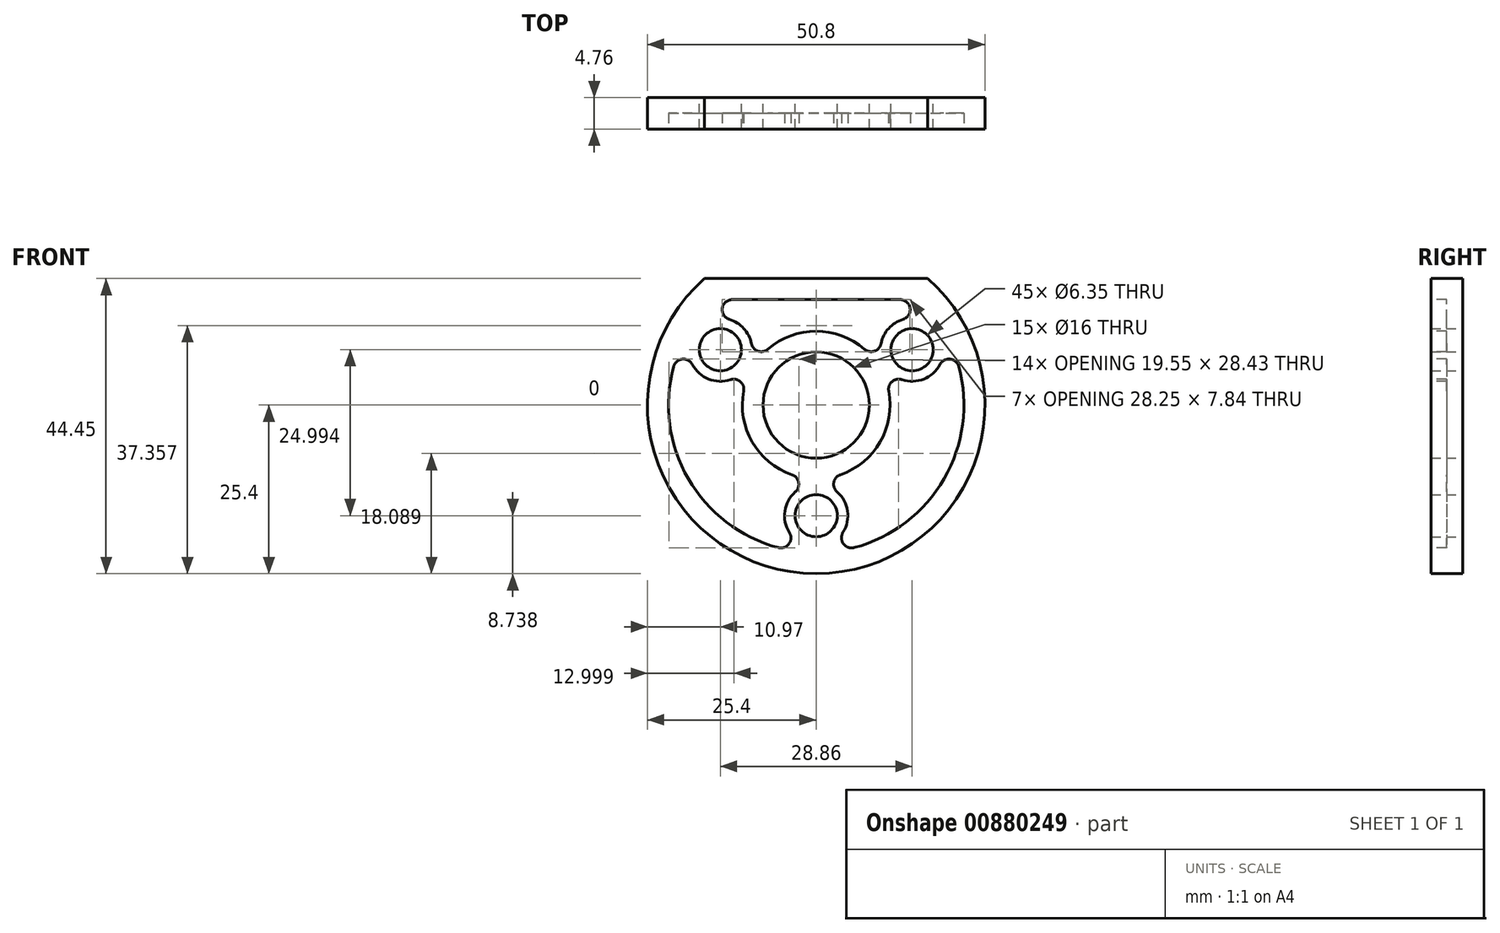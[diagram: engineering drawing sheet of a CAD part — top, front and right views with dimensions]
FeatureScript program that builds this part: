
annotation { "Feature Type Name" : "Feature", "Feature Type Description" : "" }
export const myFeature = defineFeature(function(context is Context, id is Id, definition is map)
    precondition{}
    {
        {
            var Q0;
            Q0=qCreatedBy(makeId("Front.planeOp"),FACE);
            var sketch = newSketch(context, id + "F0", { "sketchPlane" : qUnion([Q0])});
            skCircle(sketch, "E0", {"center": v(0, 0) * mm, "radius": 16.66 * mm, "construction": true});
            skCircle(sketch, "E1", {"center": v(-14.43, 8.33) * mm, "radius": 3.18 * mm});
            skCircle(sketch, "E2", {"center": v(14.43, 8.33) * mm, "radius": 3.18 * mm});
            skCircle(sketch, "E3", {"center": v(0, -16.66) * mm, "radius": 3.18 * mm});
            skCircle(sketch, "E4", {"center": v(0, 0) * mm, "radius": 25.4 * mm});
            skCircle(sketch, "E5", {"center": v(0, 0) * mm, "radius": 8 * mm});
            skLineSegment(sketch, "E6", {"start": v(-14.43, 8.33) * mm, "end": v(0, -16.66) * mm, "construction": true});
            skLineSegment(sketch, "E7", {"start": v(14.43, 8.33) * mm, "end": v(0, -16.66) * mm, "construction": true});
            skLineSegment(sketch, "E8", {"start": v(14.43, 8.33) * mm, "end": v(-14.43, 8.33) * mm, "construction": true});
            skSolve(sketch);
        }
        {
            var Q0;
            Q0=qSketchRegion(id+"F0",true);
            extrude(context, id + "F1", {"entities" : qUnion([Q0]), "depth" : 4.76 * mm});
        }
        {
            var Q0;
            Q0=makeQuery(id+"F1.opExtrude","CAP_FACE",FACE,{"disambiguationData":[OSD([sQuery(id+"F0.wireOp",EDGE,"E1"),sQuery(id+"F0.wireOp",EDGE,"E2"),sQuery(id+"F0.wireOp",EDGE,"E3"),sQuery(id+"F0.wireOp",EDGE,"E4"),sQuery(id+"F0.wireOp",EDGE,"E5")])],"isStart":false});
            var sketch = newSketch(context, id + "F2", { "sketchPlane" : qUnion([Q0])});
            skLineSegment(sketch, "E9.bottom", {"start": v(-24.52, 33.4) * mm, "end": v(26.04, 33.4) * mm});
            skLineSegment(sketch, "E9.top", {"start": v(-24.52, 19.05) * mm, "end": v(26.04, 19.05) * mm});
            skLineSegment(sketch, "E9.left", {"start": v(-24.52, 33.4) * mm, "end": v(-24.52, 19.05) * mm});
            skLineSegment(sketch, "E9.right", {"start": v(26.04, 33.4) * mm, "end": v(26.04, 19.05) * mm});
            skSolve(sketch);
        }
        {
            var Q0;
            Q0=qSketchRegion(id+"F2",true);
            extrude(context, id + "F3", {"entities" : qUnion([Q0]), "operationType" : NewBodyOperationType.REMOVE, "oppositeDirection" : true, "depth" : 25.4 * mm});
        }
        {
            var Q0;
            Q0=makeQuery(id+"F1.opExtrude","CAP_FACE",FACE,{"disambiguationData":[OSD([sQuery(id+"F0.wireOp",EDGE,"E1"),sQuery(id+"F0.wireOp",EDGE,"E2"),sQuery(id+"F0.wireOp",EDGE,"E3"),sQuery(id+"F0.wireOp",EDGE,"E4"),sQuery(id+"F0.wireOp",EDGE,"E5")])],"isStart":false});
            var sketch = newSketch(context, id + "F4", { "sketchPlane" : qUnion([Q0])});
            skArc(sketch, "E10", {"start": v(-10.91, 2.1) * mm, "mid": v(-9.62, -5.56) * mm, "end": v(-3.65, -10.5) * mm});
            skArc(sketch, "E11", {"start": v(7.27, 8.4) * mm, "mid": v(0, 11.11) * mm, "end": v(-7.27, 8.4) * mm});
            skArc(sketch, "E12", {"start": v(3.65, -10.5) * mm, "mid": v(9.62, -5.56) * mm, "end": v(10.91, 2.1) * mm});
            skArc(sketch, "E13", {"start": v(-9.76, 9.26) * mm, "mid": v(-10.9, 11.53) * mm, "end": v(-13.06, 12.9) * mm});
            skArc(sketch, "E14", {"start": v(-18.64, 6.1) * mm, "mid": v(-16.2, 3.9) * mm, "end": v(-12.9, 3.82) * mm});
            skArc(sketch, "E15", {"start": v(-21.46, 5.79) * mm, "mid": v(-19.25, -11.11) * mm, "end": v(-5.72, -21.48) * mm});
            skArc(sketch, "E16", {"start": v(5.72, -21.48) * mm, "mid": v(19.25, -11.11) * mm, "end": v(21.46, 5.79) * mm});
            skArc(sketch, "E17.filletArc", {"start": v(-10.91, 2.1) * mm, "mid": v(-11.4, 3.53) * mm, "end": v(-12.9, 3.82) * mm});
            skArc(sketch, "E18.filletArc", {"start": v(-18.64, 6.1) * mm, "mid": v(-20.16, 6.9) * mm, "end": v(-21.46, 5.79) * mm});
            skArc(sketch, "E19.filletArc", {"start": v(-9.76, 9.26) * mm, "mid": v(-8.76, 8.12) * mm, "end": v(-7.27, 8.4) * mm});
            skArc(sketch, "E20", {"start": v(12.9, 3.82) * mm, "mid": v(16.2, 3.9) * mm, "end": v(18.64, 6.1) * mm});
            skArc(sketch, "E21", {"start": v(13.06, 12.9) * mm, "mid": v(10.9, 11.53) * mm, "end": v(9.76, 9.26) * mm});
            skArc(sketch, "E22", {"start": v(4.03, -19.2) * mm, "mid": v(4.71, -15.97) * mm, "end": v(3.14, -13.08) * mm});
            skArc(sketch, "E23", {"start": v(-3.14, -13.08) * mm, "mid": v(-4.71, -15.97) * mm, "end": v(-4.03, -19.2) * mm});
            skArc(sketch, "E24.filletArc", {"start": v(-5.72, -21.48) * mm, "mid": v(-4.1, -20.9) * mm, "end": v(-4.03, -19.2) * mm});
            skArc(sketch, "E25.filletArc", {"start": v(-3.14, -13.08) * mm, "mid": v(-2.65, -11.64) * mm, "end": v(-3.65, -10.5) * mm});
            skArc(sketch, "E26.filletArc", {"start": v(4.03, -19.2) * mm, "mid": v(4.1, -20.9) * mm, "end": v(5.72, -21.48) * mm});
            skArc(sketch, "E27.filletArc", {"start": v(3.65, -10.5) * mm, "mid": v(2.65, -11.64) * mm, "end": v(3.14, -13.08) * mm});
            skArc(sketch, "E28.filletArc", {"start": v(21.46, 5.79) * mm, "mid": v(20.16, 6.9) * mm, "end": v(18.64, 6.1) * mm});
            skArc(sketch, "E29.filletArc", {"start": v(12.9, 3.82) * mm, "mid": v(11.4, 3.53) * mm, "end": v(10.91, 2.1) * mm});
            skArc(sketch, "E30.filletArc", {"start": v(7.27, 8.4) * mm, "mid": v(8.76, 8.12) * mm, "end": v(9.76, 9.26) * mm});
            skLineSegment(sketch, "E31", {"start": v(-12.62, 15.88) * mm, "end": v(12.62, 15.88) * mm});
            skArc(sketch, "E32.filletArc", {"start": v(-12.62, 15.88) * mm, "mid": v(-14.13, 14.57) * mm, "end": v(-13.06, 12.9) * mm});
            skArc(sketch, "E33.filletArc", {"start": v(13.06, 12.9) * mm, "mid": v(14.13, 14.57) * mm, "end": v(12.62, 15.88) * mm});
            skSolve(sketch);
        }
        {
            var Q0;
            Q0=qSketchRegion(id+"F4",true);
            extrude(context, id + "F5", {"entities" : qUnion([Q0]), "operationType" : NewBodyOperationType.REMOVE, "oppositeDirection" : true, "depth" : 2.38 * mm, "offsetDistance" : 25.4 * mm});
        }
    });
